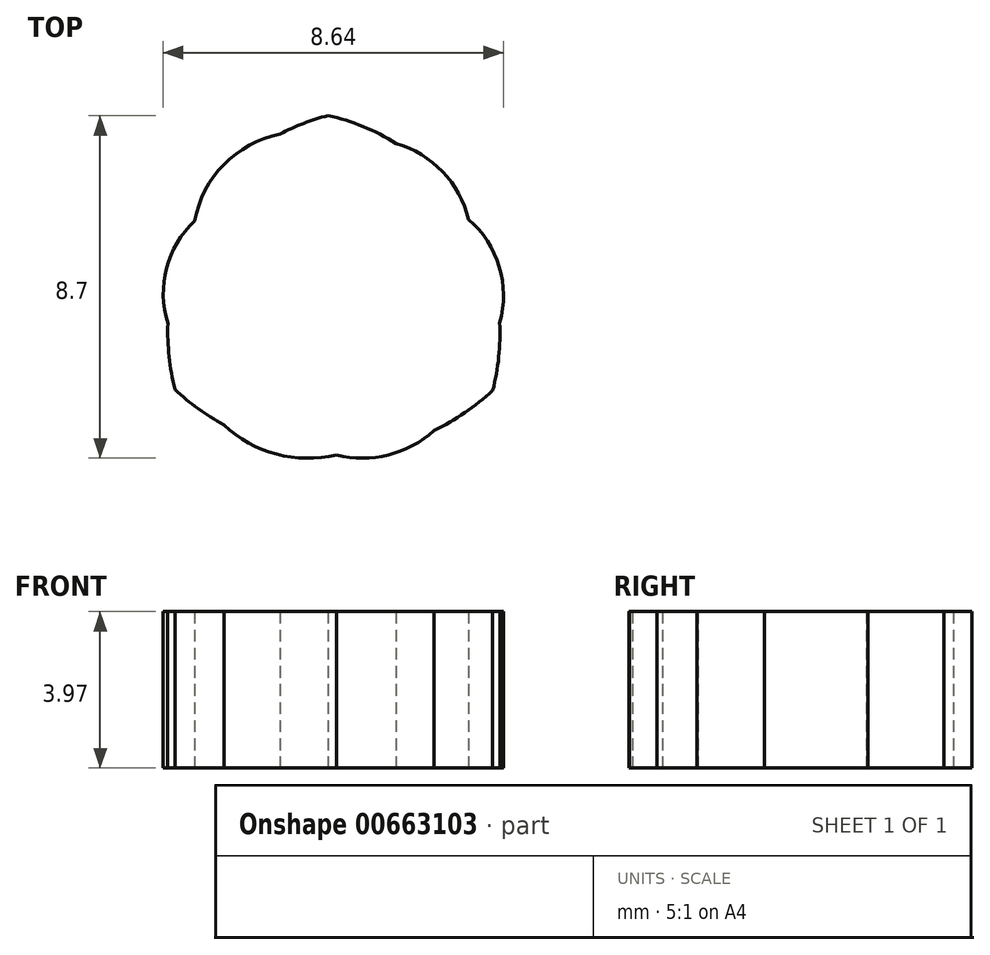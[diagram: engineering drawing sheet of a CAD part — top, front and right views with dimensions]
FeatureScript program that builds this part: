
annotation { "Feature Type Name" : "Feature", "Feature Type Description" : "" }
export const myFeature = defineFeature(function(context is Context, id is Id, definition is map)
    precondition{}
    {
        {
            var Q0;
            Q0=qCreatedBy(makeId("Top.planeOp"),FACE);
            var sketch = newSketch(context, id + "F0", { "sketchPlane" : qUnion([Q0])});
            skPoint(sketch, "E0.center", {"position": v(0, 0) * mm});
            skPoint(sketch, "E1.center", {"position": v(-0.03, 0.1) * mm});
            skLineSegment(sketch, "E2", {"start": v(-12.37, 4.64) * mm, "end": v(-12.37, 4.57) * mm});
            skLineSegment(sketch, "E3", {"start": v(7.76, 1.05) * mm, "end": v(7.76, 1.05) * mm});
            skLineSegment(sketch, "E4", {"start": v(8, -1.42) * mm, "end": v(8, -1.42) * mm});
            skLineSegment(sketch, "E5", {"start": v(6.33, 3.65) * mm, "end": v(6.36, 3.6) * mm});
            skArc(sketch, "E6", {"start": v(-4.1, -2.33) * mm, "mid": v(-3.51, -2.81) * mm, "end": v(-2.86, -3.23) * mm});
            skArc(sketch, "E7", {"start": v(2.48, -3.37) * mm, "mid": v(3.26, -2.92) * mm, "end": v(3.97, -2.35) * mm});
            skArc(sketch, "E8", {"start": v(-2.86, -3.23) * mm, "mid": v(-1.53, -3.97) * mm, "end": v(0, -4) * mm});
            skArc(sketch, "E9", {"start": v(0, -4) * mm, "mid": v(1.32, -3.99) * mm, "end": v(2.48, -3.37) * mm});
            skArc(sketch, "E10", {"start": v(-4.28, -0.65) * mm, "mid": v(-4.25, -1.5) * mm, "end": v(-4.1, -2.33) * mm});
            skArc(sketch, "E11", {"start": v(-3.6, 1.96) * mm, "mid": v(-4.32, 0.75) * mm, "end": v(-4.28, -0.65) * mm});
            skArc(sketch, "E12", {"start": v(-0.21, 4.63) * mm, "mid": v(-0.84, 4.43) * mm, "end": v(-1.43, 4.16) * mm});
            skArc(sketch, "E13", {"start": v(-1.43, 4.16) * mm, "mid": v(-2.86, 3.4) * mm, "end": v(-3.6, 1.96) * mm});
            skArc(sketch, "E14", {"start": v(1.52, 3.92) * mm, "mid": v(0.68, 4.35) * mm, "end": v(-0.21, 4.63) * mm});
            skArc(sketch, "E15", {"start": v(3.36, 2) * mm, "mid": v(2.7, 3.2) * mm, "end": v(1.52, 3.92) * mm});
            skArc(sketch, "E16", {"start": v(3.97, -2.35) * mm, "mid": v(4.12, -1.5) * mm, "end": v(4.15, -0.64) * mm});
            skArc(sketch, "E17", {"start": v(4.15, -0.64) * mm, "mid": v(4.14, 0.8) * mm, "end": v(3.36, 2) * mm});
            skSolve(sketch);
        }
        {
            var Q0;
            Q0=makeQuery(id+"F0.imprint","IMPRINT",FACE,{"disambiguationData":[TD([[makeQuery(id+"F0.imprint","IMPRINT",EDGE,{"derivedFrom":sQuery(id+"F0.wireOp",EDGE,"E6")}),1.0]])]});
            extrude(context, id + "F1", {"entities" : qUnion([Q0]), "depth" : 3.97 * mm, "offsetDistance" : 25.4 * mm});
        }
    });
